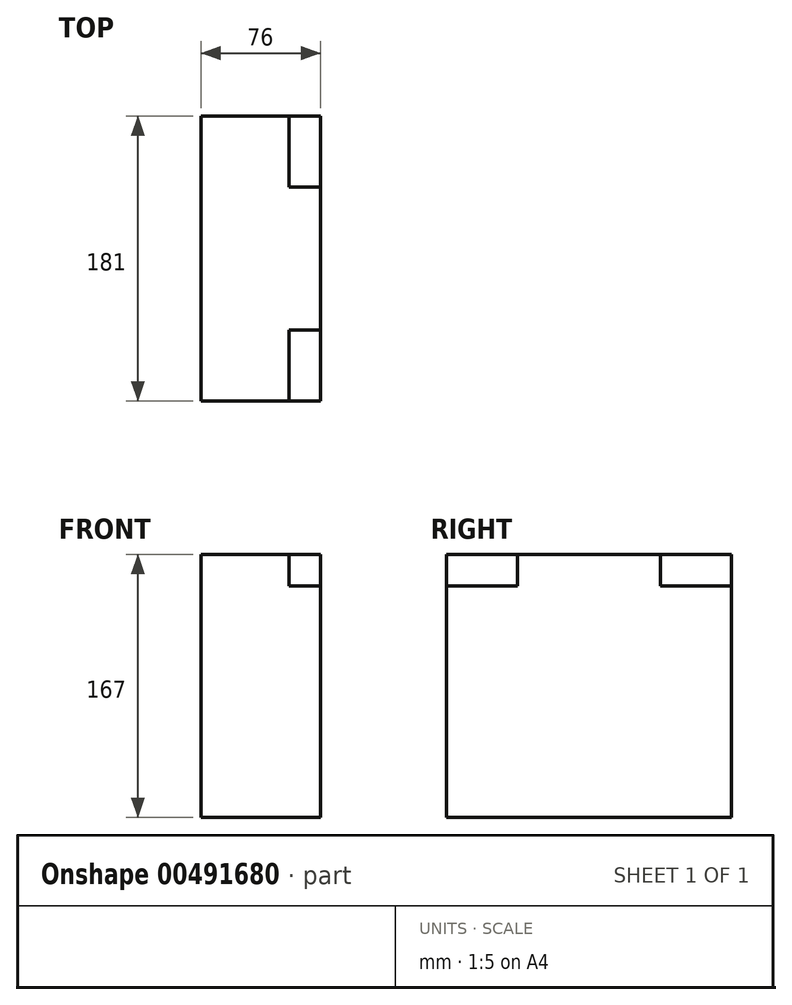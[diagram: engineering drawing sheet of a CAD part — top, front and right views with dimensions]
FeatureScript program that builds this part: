
annotation { "Feature Type Name" : "Feature", "Feature Type Description" : "" }
export const myFeature = defineFeature(function(context is Context, id is Id, definition is map)
    precondition{}
    {
        {
            var Q0;
            Q0=qCreatedBy(makeId("Right.planeOp"),FACE);
            var sketch = newSketch(context, id + "F0", { "sketchPlane" : qUnion([Q0])});
            skLineSegment(sketch, "E0.bottom", {"start": v(-91.62, -62.62) * mm, "end": v(89.38, -62.62) * mm});
            skLineSegment(sketch, "E0.top", {"start": v(-91.62, 104.38) * mm, "end": v(89.38, 104.38) * mm});
            skLineSegment(sketch, "E0.left", {"start": v(-91.62, -62.62) * mm, "end": v(-91.62, 104.38) * mm});
            skLineSegment(sketch, "E0.right", {"start": v(89.38, -62.62) * mm, "end": v(89.38, 104.38) * mm});
            skSolve(sketch);
        }
        {
            var Q0;
            Q0 = qSketchRegion(id + "F0", true);
            extrude(context, id + "F1", {"entities" : qUnion([Q0]), "depth" : 76 * mm});
        }
        {
            var Q0;
            Q0=makeQuery(id+"F1.opExtrude","CAP_FACE",FACE,{"disambiguationData":[OSD([sQuery(id+"F0.wireOp",EDGE,"E0.bottom"),sQuery(id+"F0.wireOp",EDGE,"E0.top"),sQuery(id+"F0.wireOp",EDGE,"E0.left"),sQuery(id+"F0.wireOp",EDGE,"E0.right")])],"isStart":false});
            var sketch = newSketch(context, id + "F2", { "sketchPlane" : qUnion([Q0])});
            skLineSegment(sketch, "E1.bottom", {"start": v(-91.62, 84.38) * mm, "end": v(-46.62, 84.38) * mm});
            skLineSegment(sketch, "E1.top", {"start": v(-91.62, 104.38) * mm, "end": v(-46.62, 104.38) * mm});
            skLineSegment(sketch, "E1.left", {"start": v(-91.62, 84.38) * mm, "end": v(-91.62, 104.38) * mm});
            skLineSegment(sketch, "E1.right", {"start": v(-46.62, 84.38) * mm, "end": v(-46.62, 104.38) * mm});
            skSolve(sketch);
        }
        {
            var Q0;
            Q0=makeQuery(id+"F2.imprint","IMPRINT",FACE,{"disambiguationData":[TD([[makeQuery(id+"F2.imprint","IMPRINT",EDGE,{"derivedFrom":sQuery(id+"F2.wireOp",EDGE,"E1.bottom")}),1.0]])]});
            extrude(context, id + "F3", {"entities" : qUnion([Q0]), "operationType" : NewBodyOperationType.REMOVE, "oppositeDirection" : true, "depth" : 20 * mm});
        }
        {
            var Q0;
            Q0=makeQuery(id+"F1.opExtrude","CAP_FACE",FACE,{"disambiguationData":[OSD([sQuery(id+"F0.wireOp",EDGE,"E0.bottom"),sQuery(id+"F0.wireOp",EDGE,"E0.top"),sQuery(id+"F0.wireOp",EDGE,"E0.left"),sQuery(id+"F0.wireOp",EDGE,"E0.right")])],"isStart":false});
            var sketch = newSketch(context, id + "F4", { "sketchPlane" : qUnion([Q0])});
            skLineSegment(sketch, "E2.bottom", {"start": v(89.38, 84.38) * mm, "end": v(44.38, 84.38) * mm});
            skLineSegment(sketch, "E2.top", {"start": v(89.38, 104.38) * mm, "end": v(44.38, 104.38) * mm});
            skLineSegment(sketch, "E2.left", {"start": v(89.38, 84.38) * mm, "end": v(89.38, 104.38) * mm});
            skLineSegment(sketch, "E2.right", {"start": v(44.38, 84.38) * mm, "end": v(44.38, 104.38) * mm});
            skSolve(sketch);
        }
        {
            var Q0;
            Q0 = qSketchRegion(id + "F4", true);
            extrude(context, id + "F5", {"entities" : qUnion([Q0]), "operationType" : NewBodyOperationType.REMOVE, "oppositeDirection" : true, "depth" : 20 * mm});
        }
    });
